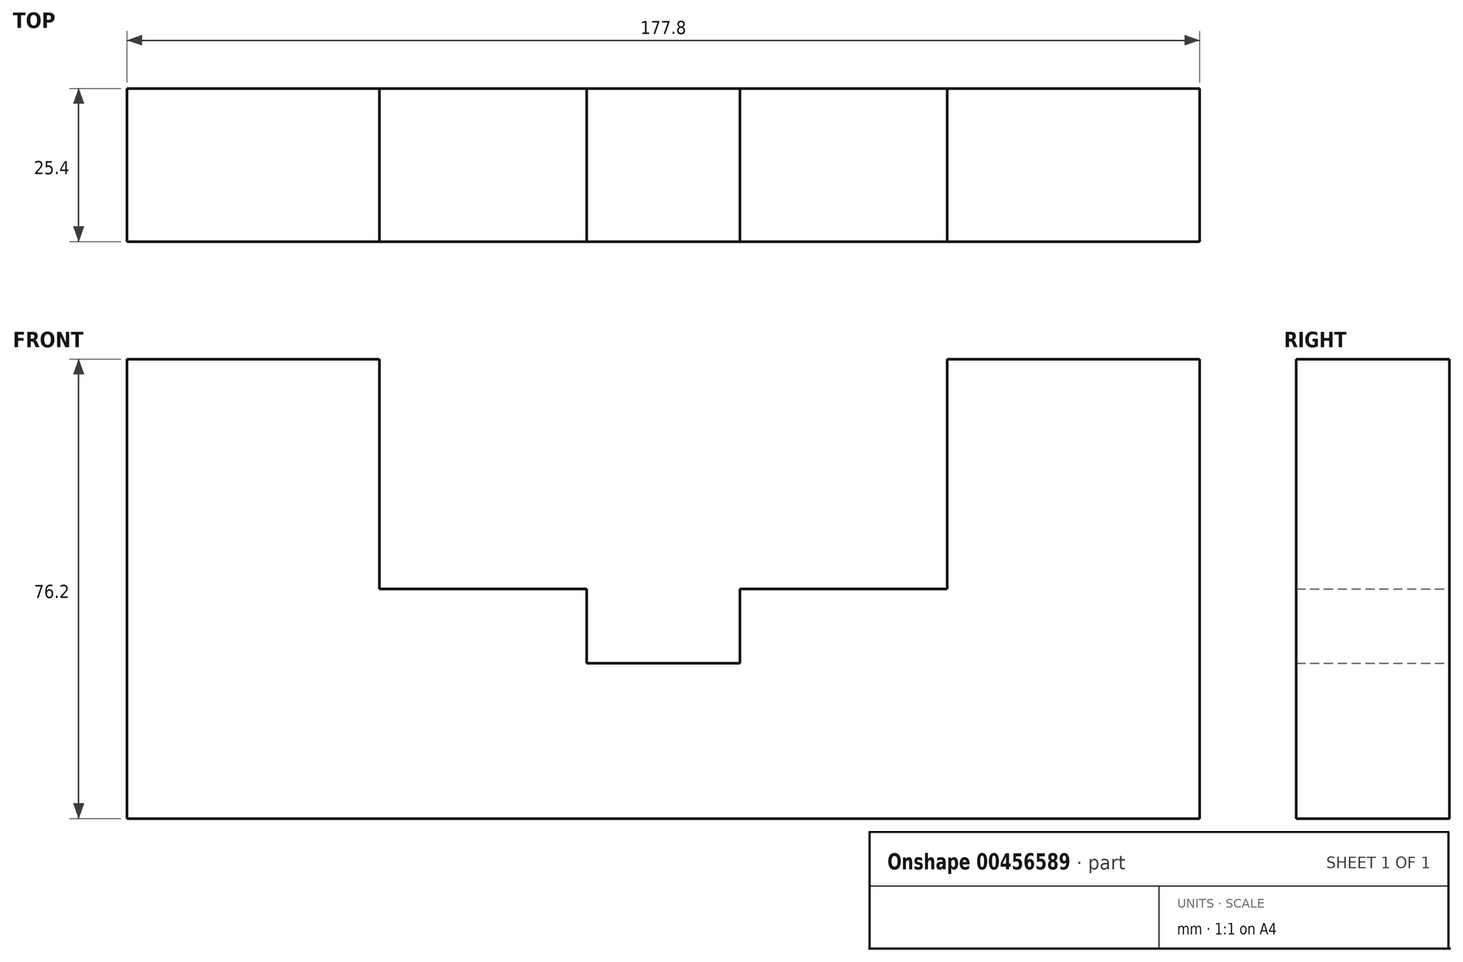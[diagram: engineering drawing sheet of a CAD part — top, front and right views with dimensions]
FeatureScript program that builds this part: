
annotation { "Feature Type Name" : "Feature", "Feature Type Description" : "" }
export const myFeature = defineFeature(function(context is Context, id is Id, definition is map)
    precondition{}
    {
        {
            var Q0;
            Q0=qCreatedBy(makeId("Front.planeOp"),FACE);
            var sketch = newSketch(context, id + "F0", { "sketchPlane" : qUnion([Q0])});
            skLineSegment(sketch, "E0.bottom", {"start": v(-88.9, 25.02) * mm, "end": v(-47.05, 25.02) * mm});
            skLineSegment(sketch, "E0.top", {"start": v(-88.9, -51.18) * mm, "end": v(-41.57, -51.18) * mm});
            skLineSegment(sketch, "E0.left", {"start": v(-88.9, 25.02) * mm, "end": v(-88.9, -51.18) * mm});
            skLineSegment(sketch, "E0.right", {"start": v(-47.05, 25.02) * mm, "end": v(-47.05, -13.08) * mm});
            skLineSegment(sketch, "E1.bottom", {"start": v(-47.05, -13.08) * mm, "end": v(0, -13.08) * mm});
            skLineSegment(sketch, "E1.top", {"start": v(-88.9, -51.18) * mm, "end": v(0, -51.18) * mm});
            skLineSegment(sketch, "E1.left", {"start": v(-88.9, -30.67) * mm, "end": v(-88.9, -51.18) * mm});
            skLineSegment(sketch, "E2.filletArc", {"start": v(-47.05, -13.08) * mm, "end": v(-47.05, -13.08) * mm});
            skLineSegment(sketch, "E3.MirrorCS", {"start": v(47.05, 25.02) * mm, "end": v(47.05, -13.08) * mm});
            skLineSegment(sketch, "E4.MirrorCS", {"start": v(88.9, 25.02) * mm, "end": v(47.05, 25.02) * mm});
            skLineSegment(sketch, "E5.MirrorCS", {"start": v(88.9, 25.02) * mm, "end": v(88.9, -51.18) * mm});
            skLineSegment(sketch, "E6.MirrorCS", {"start": v(47.05, -13.08) * mm, "end": v(0, -13.08) * mm});
            skLineSegment(sketch, "E7.MirrorCS", {"start": v(88.9, -51.18) * mm, "end": v(0, -51.18) * mm});
            skLineSegment(sketch, "E8.MirrorCS", {"start": v(47.05, -13.08) * mm, "end": v(47.05, -13.08) * mm});
            skSolve(sketch);
        }
        {
            var Q0;
            Q0 = qSketchRegion(id + "F0", true);
            extrude(context, id + "F1", {"entities" : qUnion([Q0]), "depth" : 25.4 * mm});
        }
        {
            var Q0;
            Q0=qCreatedBy(makeId("Front.planeOp"),FACE);
            var sketch = newSketch(context, id + "F2", { "sketchPlane" : qUnion([Q0])});
            skLineSegment(sketch, "E9.bottom", {"start": v(-12.7, -13.08) * mm, "end": v(12.7, -13.08) * mm});
            skLineSegment(sketch, "E9.top", {"start": v(-12.7, -25.4) * mm, "end": v(12.7, -25.4) * mm});
            skLineSegment(sketch, "E9.left", {"start": v(-12.7, -13.08) * mm, "end": v(-12.7, -25.4) * mm});
            skLineSegment(sketch, "E9.right", {"start": v(12.7, -13.08) * mm, "end": v(12.7, -25.4) * mm});
            skSolve(sketch);
        }
        {
            var Q0;
            Q0 = qSketchRegion(id + "F2", true);
            extrude(context, id + "F3", {"entities" : qUnion([Q0]), "operationType" : NewBodyOperationType.REMOVE, "depth" : 4 * mm});
        }
        {
            var Q0;
            Q0 = qSketchRegion(id + "F2", true);
            extrude(context, id + "F4", {"entities" : qUnion([Q0]), "operationType" : NewBodyOperationType.REMOVE, "endBound" : BoundingType.THROUGH_ALL, "depth" : 25 * mm});
        }
    });
